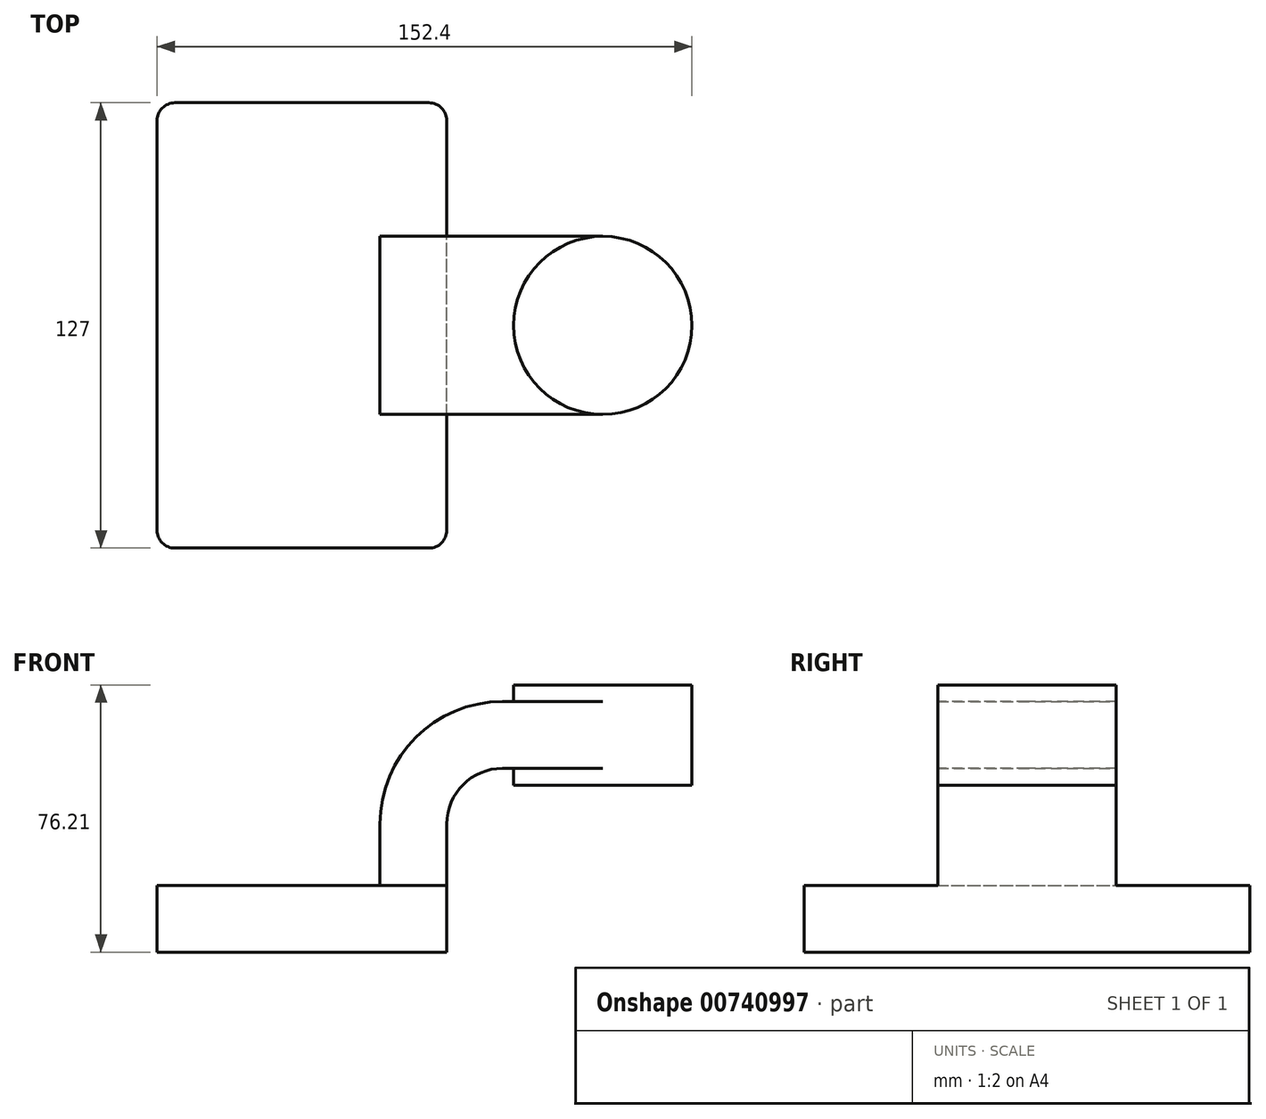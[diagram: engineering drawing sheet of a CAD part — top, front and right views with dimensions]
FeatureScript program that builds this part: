
annotation { "Feature Type Name" : "Feature", "Feature Type Description" : "" }
export const myFeature = defineFeature(function(context is Context, id is Id, definition is map)
    precondition{}
    {
        {
            var Q0;
            Q0=qCreatedBy(makeId("Front.planeOp"),FACE);
            var sketch = newSketch(context, id + "F0", { "sketchPlane" : qUnion([Q0])});
            skLineSegment(sketch, "E0.bottom", {"start": v(41.28, -9.52) * mm, "end": v(-41.28, -9.52) * mm});
            skLineSegment(sketch, "E0.top", {"start": v(41.27, 9.53) * mm, "end": v(-41.28, 9.53) * mm});
            skLineSegment(sketch, "E0.left", {"start": v(41.28, -9.52) * mm, "end": v(41.28, 9.53) * mm});
            skLineSegment(sketch, "E0.right", {"start": v(-41.28, -9.52) * mm, "end": v(-41.28, 9.53) * mm});
            skPoint(sketch, "E0.middle", {"position": v(0, 0) * mm});
            skLineSegment(sketch, "E1.bottom", {"start": v(60.32, 38.1) * mm, "end": v(111.12, 38.1) * mm});
            skLineSegment(sketch, "E1.top", {"start": v(60.32, 66.68) * mm, "end": v(111.12, 66.68) * mm});
            skLineSegment(sketch, "E1.left", {"start": v(60.32, 38.1) * mm, "end": v(60.32, 66.68) * mm});
            skLineSegment(sketch, "E1.right", {"start": v(111.12, 38.1) * mm, "end": v(111.12, 66.68) * mm});
            skPoint(sketch, "E1.middle", {"position": v(85.72, 52.39) * mm});
            skLineSegment(sketch, "E2", {"start": v(41.27, 9.53) * mm, "end": v(41.27, 27) * mm});
            skArc(sketch, "E3", {"start": v(41.27, 27) * mm, "mid": v(45.92, 38.23) * mm, "end": v(57.15, 42.88) * mm});
            skLineSegment(sketch, "E4", {"start": v(57.15, 42.88) * mm, "end": v(85.72, 42.88) * mm});
            skLineSegment(sketch, "E5.0", {"start": v(57.15, 61.93) * mm, "end": v(85.72, 61.93) * mm});
            skArc(sketch, "E5.1", {"start": v(22.23, 27) * mm, "mid": v(32.45, 51.7) * mm, "end": v(57.15, 61.93) * mm});
            skLineSegment(sketch, "E5.2", {"start": v(22.22, 9.53) * mm, "end": v(22.22, 27) * mm});
            skLineSegment(sketch, "E6", {"start": v(85.72, 38.1) * mm, "end": v(85.72, 66.68) * mm});
            skFitSpline(sketch, "E7", {"points": [v(-41.28, 9.52) * mm, v(57.15, 61.93) * mm], "startDerivative": vector(0.21, 145.24) * mm, "endDerivative": vector(104.3, -1.84) * mm});
            skSolve(sketch);
        }
        {
            var Q0;
            Q0=makeQuery(id+"F0.imprint","IMPRINT",FACE,{"disambiguationData":[TD([[makeQuery(id+"F0.imprint","IMPRINT",EDGE,{"derivedFrom":sQuery(id+"F0.wireOp",EDGE,"E0.bottom")}),-1.0]])]});
            extrude(context, id + "F1", {"entities" : qUnion([Q0]), "endBound" : BoundingType.SYMMETRIC, "depth" : 127 * mm, "offsetDistance" : 25.4 * mm});
        }
        {
            var Q0;
            {var subQ1=sQuery(id+"F0.wireOp",EDGE,"E2");Q0=makeQuery(id+"F0.imprint","IMPRINT",FACE,{"disambiguationData":[TD([[makeQuery(id+"F0.imprint","IMPRINT",EDGE,{"derivedFrom":subQ1}),1.0]])]});}
            var Q1;
            {var subQ0=sQuery(id+"F0.wireOp",EDGE,"E4");var subQ1=sQuery(id+"F0.wireOp",EDGE,"E1.left");var subQ2=makeQuery(id+"F0.imprint","INTERSECT",VERTEX,{"derivedFrom":[subQ1,subQ0]});Q1=makeQuery(id+"F0.imprint","IMPRINT",FACE,{"disambiguationData":[TD([[makeQuery(id+"F0.imprint","IMPRINT",EDGE,{"disambiguationData":[TD([[subQ2,-1.0]])],"derivedFrom":subQ1}),-1.0]])]});}
            extrude(context, id + "F2", {"entities" : qUnion([Q0, Q1]), "operationType" : NewBodyOperationType.ADD, "endBound" : BoundingType.SYMMETRIC, "depth" : 50.8 * mm, "offsetDistance" : 25.4 * mm});
        }
        {
            var Q0;
            Q0=makeQuery(id+"F0.imprint","IMPRINT",FACE,{"disambiguationData":[TD([[makeQuery(id+"F0.imprint","IMPRINT",EDGE,{"derivedFrom":sQuery(id+"F0.wireOp",EDGE,"E5.1")}),1.0]])]});
            extrude(context, id + "F3", {"entities" : qUnion([Q0]), "operationType" : NewBodyOperationType.ADD, "endBound" : BoundingType.SYMMETRIC, "depth" : 15.88 * mm, "offsetDistance" : 25.4 * mm});
        }
        {
            var Q0;
            {var subQ0=sQuery(id+"F0.wireOp",EDGE,"E1.right");Q0=makeQuery(id+"F0.imprint","IMPRINT",FACE,{"disambiguationData":[TD([[makeQuery(id+"F0.imprint","IMPRINT",EDGE,{"derivedFrom":subQ0}),1.0]])]});}
            var Q1;
            Q1=sQuery(id+"F0.wireOp",EDGE,"E6");
            revolve(context, id + "F4", {"operationType" : NewBodyOperationType.ADD, "surfaceOperationType" : NewSurfaceOperationType.NEW, "entities" : qUnion([Q0]), "axis" : qUnion([Q1]), "revolveType" : RevolveType.FULL});
        }
        {
            var Q0;
            Q0=makeQuery(id+"F1.opExtrude","CAP_EDGE",EDGE,{"disambiguationData":[OSD([sQuery(id+"F0.wireOp",EDGE,"E0.right")])],"isStart":false});
            var Q1;
            Q1=makeQuery(id+"F1.opExtrude","CAP_EDGE",EDGE,{"disambiguationData":[OSD([sQuery(id+"F0.wireOp",EDGE,"E0.left")])],"isStart":false});
            fillet(context, id + "F5", {"entities" : qUnion([Q0, Q1]), "radius" : 5.08 * mm, "tangentPropagation" : true, "allowEdgeOverflow" : false});
        }
        {
            var Q0;
            Q0=makeQuery(id+"F1.opExtrude","CAP_EDGE",EDGE,{"disambiguationData":[OSD([sQuery(id+"F0.wireOp",EDGE,"E0.left")])],"isStart":true});
            fillet(context, id + "F6", {"entities" : qUnion([Q0]), "radius" : 5.08 * mm, "tangentPropagation" : true, "allowEdgeOverflow" : false});
        }
        {
            var Q0;
            Q0=makeQuery(id+"F1.opExtrude","CAP_EDGE",EDGE,{"disambiguationData":[OSD([sQuery(id+"F0.wireOp",EDGE,"E0.right")])],"isStart":true});
            fillet(context, id + "F7", {"entities" : qUnion([Q0]), "radius" : 5.08 * mm, "tangentPropagation" : true, "allowEdgeOverflow" : false});
        }
    });
